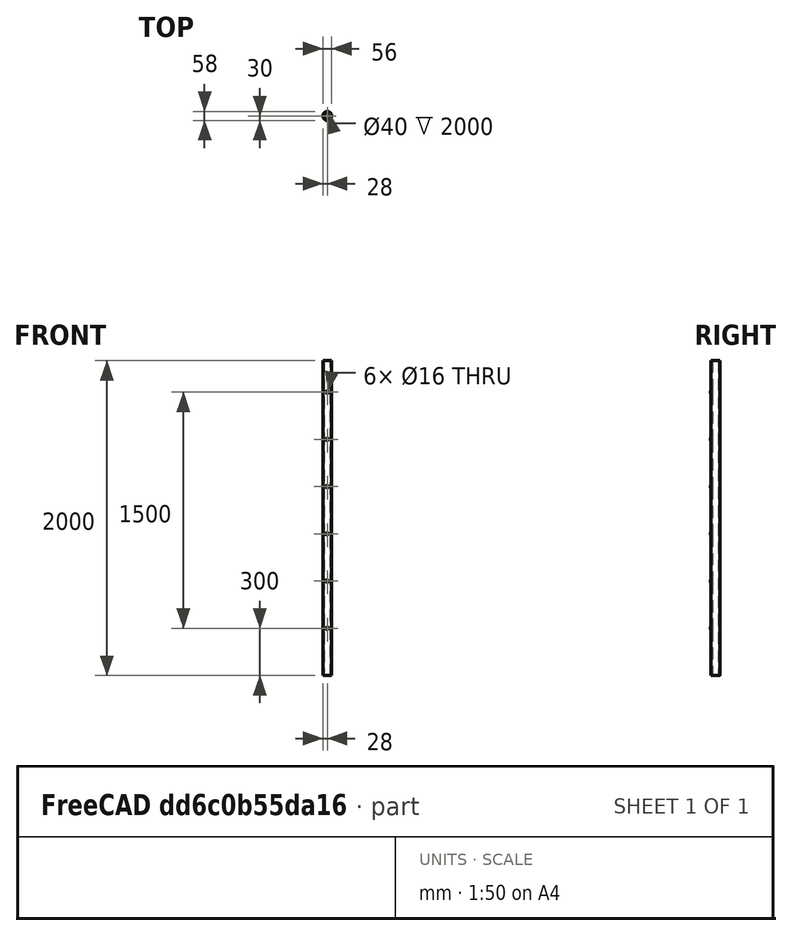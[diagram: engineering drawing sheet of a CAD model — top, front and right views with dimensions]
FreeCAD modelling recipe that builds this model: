
FCSTD DOCUMENT  (FreeCAD 1.0R39319 (Git))
Label: Final Garden Pipe
License: All rights reserved
LicenseURL: https://en.wikipedia.org/wiki/All_rights_reserved
objects: Part::Cut×10, Part::Cylinder×8, Part::FeaturePython×6, App::DocumentObjectGroupPython×2, PartDesign::Boolean×1, PartDesign::Body×1, App::MaterialObjectPython×1
note: 27 computed .brp shape members not serialized (recipe doc carries the construction recipe); baked Part::Feature solids carry a one-line shape summary decoded from their .brp

FEATURE [Part::Cylinder] Cylinder
  Angle = 360
  AttacherType = Attacher::AttachEngine3D
  FirstAngle = 0
  Height = 2000
  Radius = 20
  SecondAngle = 0
FEATURE [Part::Cylinder] Cylinder001
  Angle = 360
  AttacherType = Attacher::AttachEngine3D
  FirstAngle = 0
  Height = 2000
  Radius = 28
  SecondAngle = 0
FEATURE [Part::Cut] Cut
  Base = -> Cylinder001
  Refine = true
  Tool = -> Cylinder
FEATURE [Part::Cylinder] Cylinder002
  Angle = 360
  AttacherType = Attacher::AttachEngine3D
  FirstAngle = 0
  Height = 30
  Placement = pos=(0,0,300) rot=(1,0,0;1.5708rad)
  Radius = 8
  SecondAngle = 0
FEATURE [Part::Cut] Cut001
  Base = -> Cut
  Refine = true
  Tool = -> Cylinder002
FEATURE [Part::Cylinder] Cylinder004 .. Cylinder008  x5 (patterned run collapsed; names and placements below)
  Angle = 360
  AttacherType = Attacher::AttachEngine3D
  FirstAngle = 0
  Height = 30
  Radius = 8
  SecondAngle = 0
  placements: 5 in arithmetic series — first pos=(0,0,600) rot=(1,0,0;1.5708rad), step (0,0,300), last pos=(0,0,1800) rot=(1,0,0;1.5708rad)
FEATURE [Part::Cut] Cut003
  Base = -> Cut001
  Refine = true
  Tool = -> Cylinder002
FEATURE [Part::Cut] Cut004
  Base = -> Cut003
  Refine = true
  Tool = -> Cylinder005
FEATURE [Part::Cut] Cut005
  Base = -> Cut004
  Refine = true
  Tool = -> Cylinder007
FEATURE [Part::Cut] Cut006
  Base = -> Cut005
  Refine = true
  Tool = -> Cylinder006
FEATURE [Part::Cut] Cut007
  Base = -> Cut006
  Refine = true
  Tool = -> Cylinder008
FEATURE [Part::Cut] Cut008
  Base = -> Cut007
  Refine = true
  Tool = -> Cylinder004
FEATURE [Part::Cut] Cut009
  Base = -> Cut008
  Refine = true
  Tool = -> Cylinder004
FEATURE [Part::Cut] Cut010
  Base = -> Cut009
  Refine = true
  Tool = -> Cylinder004
FEATURE [PartDesign::Boolean] Boolean
  Group = -> [Cut,Cut004,Cut001,Cut003,Cylinder001,Cylinder,Cylinder002,Cylinder004,Cylinder005,Cylinder006,Cylinder007,Cylinder008,Cut008,Cut006,Cut009,Cut007,Cut010,Cut005]
  Refine = true
  Suppressed = false
  Type = 1
  UsePlacement = true
FEATURE [PartDesign::Body] Body
  AllowCompound = false
  Group = -> [Boolean]
  Origin = -> Origin
  Tip = -> Boolean
FEATURE [Part::FeaturePython] PhysicsModel  # WARN: FeaturePython — macro-defined, semantics opaque (R4)
  Flow = 0
  Phase = 0
  SRFModelAxis = (0,0,0)
  SRFModelCoR = (0,0,0)
  SRFModelEnabled = false
  SRFModelRPM = 0
  Time = 0
  Turbulence = 1
  TurbulenceModel = 0
  gx = 0
  gy = -9800
  gz = 0
FEATURE [App::MaterialObjectPython] FluidProperties  label="Water"  # material (typed FeaturePython)
  Category = 1
  Material = CardName=WaterIsothermal,Density=998 kg/m^3,Description=Standard distilled water properties at 20 Degrees Celsius and 1 atm,+3 more (map truncated)
FEATURE [Part::FeaturePython] CfdSolver  # WARN: FeaturePython — macro-defined, semantics opaque (R4)
  ConvergenceTol = 0.001
  EndTime = 1
  InputCaseName = case
  MaxCFLNumber = 5
  MaxInterfaceCFLNumber = 5
  MaxIterations = 2000
  Parallel = true
  ParallelCores = 4
  PurgeWrite = 0
  StartFrom = 0
  SteadyWriteInterval = 100
  TimeStep = 0.001
  TransientWriteInterval = 0.1
FEATURE [App::DocumentObjectGroupPython] Boolean_Mesh  # scripted group (container) (typed FeaturePython)
  CaseName = meshCase
  CellsBetweenLevels = 3
  CharacteristicLengthMax = 20
  ConvertToDualMesh = false
  EdgeRefinement = 1
  ElementDimension = 1
  ImplicitEdgeDetection = false
  MeshUtility = 1
  NumberOfProcesses = 1
  NumberOfThreads = 0
  Part = -> Boolean
  PointInMesh = x=0.0 mm; y=0.0 mm; z=1.0 mm
  STLAngularMeshDensity = 100
  STLRelativeLinearDeflection = 0.001
FEATURE [Part::FeaturePython] CfdFluidBoundary  label="inlet"  # WARN: FeaturePython — macro-defined, semantics opaque (R4)
  AngularVelocity = 0
  BoundarySubType = 6
  BoundaryType = 1
  DefaultBoundary = false
  DissipationRate = 50000000
  HeatFlux = 0
  HeatTransferCoeff = 0
  Intermittency = 1
  MassFlowRate = 0
  NuTilda = 55000000
  PeriodicCentreOfRotation = (0,0,0)
  PeriodicCentreOfRotationAxis = (0,0,0)
  PeriodicMaster = true
  PeriodicSeparationVector = (0,0,0)
  PorousBaffleMethod = 0
  Power = 0
  Pressure = 101.1
  PressureDropCoeff = 0
  ReThetat = 1
  RelativeToFrame = false
  ReverseNormal = false
  RotationAxis = (0,0,1)
  RotationOrigin = (0,0,0)
  RotationalPeriodic = false
  RoughnessConstant = 0.5
  RoughnessHeight = 0
  ScreenSpacing = 2
  ScreenWireDiameter = 0.2
  ShapeRefs = -> [Boolean]
  SlipRatio = 0
  SpecificDissipationRate = 1
  Temperature = 290
  ThermalBoundaryType = 0
  TurbulenceInletSpecification = 4
  TurbulenceIntensityPercentage = 1
  TurbulenceLengthScale = 100
  TurbulentKineticEnergy = 10000
  TurbulentViscosity = 50000000
  Ux = 0
  Uy = 0
  Uz = 1000
  VelocityIsCartesian = true
  VelocityMag = 0
  VolFlowRate = 0
  kEqnTurbulentKineticEnergy = 10000
  kEqnTurbulentViscosity = 50000000
FEATURE [Part::FeaturePython] InitialiseFields  # WARN: FeaturePython — macro-defined, semantics opaque (R4)
  BoundaryU = -> CfdFluidBoundary
  PotentialFlow = false
  PotentialFlowP = false
  Pressure = 0.1
  ReThetat = 1
  Temperature = 290
  UseInletTemperatureValue = false
  UseInletTurbulenceValues = false
  UseInletUValues = true
  UseOutletPValue = false
  Ux = 0
  Uy = 0
  Uz = 0
  epsilon = 50000000
  gammaInt = 1
  k = 10000
  nuTilda = 55000000
  nut = 50000000
  omega = 1
FEATURE [Part::FeaturePython] CfdFluidBoundary002  label="wall001"  # WARN: FeaturePython — macro-defined, semantics opaque (R4)
  AngularVelocity = 0
  BoundarySubType = 0
  BoundaryType = 0
  DefaultBoundary = false
  DissipationRate = 50000000
  HeatFlux = 0
  HeatTransferCoeff = 0
  Intermittency = 1
  MassFlowRate = 0
  NuTilda = 55000000
  PeriodicCentreOfRotation = (0,0,0)
  PeriodicCentreOfRotationAxis = (0,0,0)
  PeriodicMaster = true
  PeriodicSeparationVector = (0,0,0)
  PorousBaffleMethod = 0
  Power = 0
  Pressure = 100
  PressureDropCoeff = 0
  ReThetat = 1
  RelativeToFrame = false
  ReverseNormal = false
  RotationAxis = (0,0,1)
  RotationOrigin = (0,0,0)
  RotationalPeriodic = false
  RoughnessConstant = 0.5
  RoughnessHeight = 0
  ScreenSpacing = 2
  ScreenWireDiameter = 0.2
  ShapeRefs = -> [Boolean]
  SlipRatio = 0
  SpecificDissipationRate = 1
  Temperature = 290
  ThermalBoundaryType = 0
  TurbulenceInletSpecification = 4
  TurbulenceIntensityPercentage = 1
  TurbulenceLengthScale = 100
  TurbulentKineticEnergy = 10000
  TurbulentViscosity = 50000000
  Ux = 0
  Uy = 0
  Uz = 0
  VelocityIsCartesian = true
  VelocityMag = 0
  VolFlowRate = 0
  kEqnTurbulentKineticEnergy = 10000
  kEqnTurbulentViscosity = 50000000
FEATURE [Part::FeaturePython] CfdFluidBoundary003  label="outlet"  # WARN: FeaturePython — macro-defined, semantics opaque (R4)
  AngularVelocity = 0
  BoundarySubType = 11
  BoundaryType = 2
  DefaultBoundary = false
  DissipationRate = 50000000
  HeatFlux = 0
  HeatTransferCoeff = 0
  Intermittency = 1
  MassFlowRate = 0
  NuTilda = 55000000
  PeriodicCentreOfRotation = (0,0,0)
  PeriodicCentreOfRotationAxis = (0,0,0)
  PeriodicMaster = true
  PeriodicSeparationVector = (0,0,0)
  PorousBaffleMethod = 0
  Power = 0
  Pressure = 100
  PressureDropCoeff = 0
  ReThetat = 1
  RelativeToFrame = false
  ReverseNormal = false
  RotationAxis = (0,0,1)
  RotationOrigin = (0,0,0)
  RotationalPeriodic = false
  RoughnessConstant = 0.5
  RoughnessHeight = 0
  ScreenSpacing = 2
  ScreenWireDiameter = 0.2
  ShapeRefs = -> [Boolean]
  SlipRatio = 0
  SpecificDissipationRate = 1
  Temperature = 290
  ThermalBoundaryType = 0
  TurbulenceInletSpecification = 4
  TurbulenceIntensityPercentage = 1
  TurbulenceLengthScale = 100
  TurbulentKineticEnergy = 10000
  TurbulentViscosity = 50000000
  Ux = 0
  Uy = 0
  Uz = 0
  VelocityIsCartesian = true
  VelocityMag = 0
  VolFlowRate = 0
  kEqnTurbulentKineticEnergy = 10000
  kEqnTurbulentViscosity = 50000000
FEATURE [App::DocumentObjectGroupPython] CfdAnalysis  # scripted group (container) (typed FeaturePython)
  Group = -> [PhysicsModel,FluidProperties,InitialiseFields,CfdSolver,Boolean_Mesh,CfdFluidBoundary,CfdFluidBoundary002,CfdFluidBoundary003]
  HostfileName = ../mpi_hostfile
  IsActiveAnalysis = true
  NeedsCaseRewrite = false
  NeedsMeshRerun = false
  NeedsMeshRewrite = false
  UseHostfile = false
